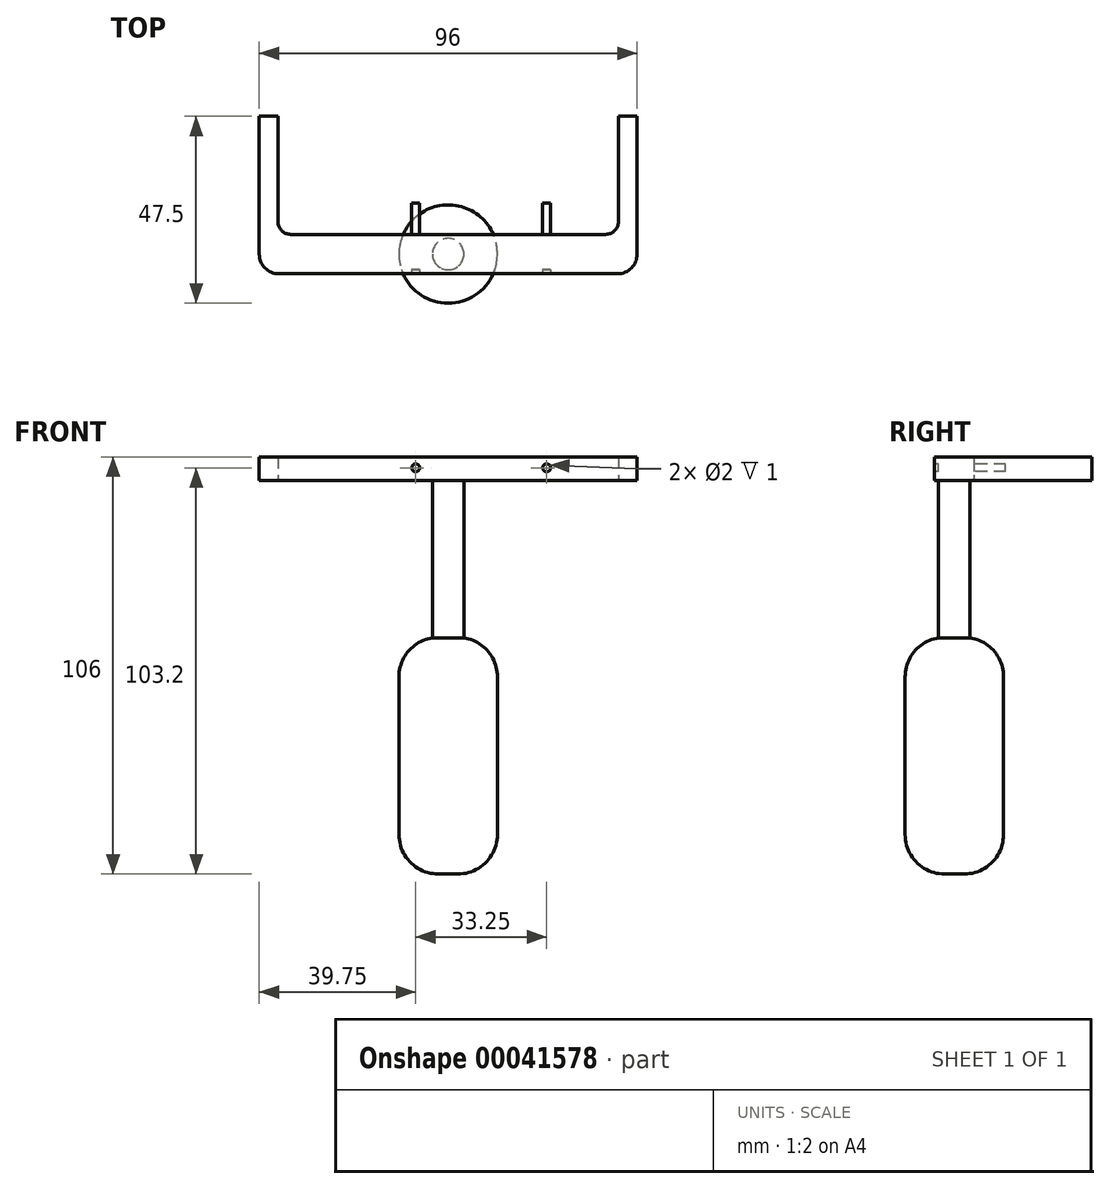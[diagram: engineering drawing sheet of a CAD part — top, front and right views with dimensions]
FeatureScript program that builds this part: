
annotation { "Feature Type Name" : "Feature", "Feature Type Description" : "" }
export const myFeature = defineFeature(function(context is Context, id is Id, definition is map)
    precondition{}
    {
        {
            var Q0;
            Q0=qCreatedBy(makeId("Top.planeOp"),FACE);
            var sketch = newSketch(context, id + "F0", { "sketchPlane" : qUnion([Q0])});
            skLineSegment(sketch, "E0.top", {"start": v(-48, -45) * mm, "end": v(48, -45) * mm});
            skLineSegment(sketch, "E0.left", {"start": v(-48, -5) * mm, "end": v(-48, -45) * mm});
            skLineSegment(sketch, "E0.right", {"start": v(48, -5) * mm, "end": v(48, -45) * mm});
            skLineSegment(sketch, "E1.top", {"start": v(-43.25, -35) * mm, "end": v(43.25, -35) * mm});
            skLineSegment(sketch, "E1.left", {"start": v(-43.25, -5) * mm, "end": v(-43.25, -35) * mm});
            skLineSegment(sketch, "E1.right", {"start": v(43.25, -5) * mm, "end": v(43.25, -35) * mm});
            skLineSegment(sketch, "E2", {"start": v(-43.25, -5) * mm, "end": v(-48, -5) * mm});
            skLineSegment(sketch, "E3", {"start": v(43.25, -5) * mm, "end": v(48, -5) * mm});
            skSolve(sketch);
        }
        {
            var Q0;
            Q0=makeQuery(id+"F0.imprint","IMPRINT",FACE,{"disambiguationData":[TD([[makeQuery(id+"F0.imprint","IMPRINT",EDGE,{"derivedFrom":sQuery(id+"F0.wireOp",EDGE,"E0.top")}),1.0]])]});
            extrude(context, id + "F1", {"entities" : qUnion([Q0]), "depth" : 6 * mm});
        }
        {
            var Q0;
            Q0=makeQuery(id+"F1.opExtrude","SWEPT_EDGE",EDGE,{"disambiguationData":[OSD([sQuery(id+"F0.wireOp",EDGE,"E1.top"),sQuery(id+"F0.wireOp",EDGE,"E1.left")])]});
            var Q1;
            Q1=makeQuery(id+"F1.opExtrude","SWEPT_EDGE",EDGE,{"disambiguationData":[OSD([sQuery(id+"F0.wireOp",EDGE,"E1.top"),sQuery(id+"F0.wireOp",EDGE,"E1.right")])]});
            fillet(context, id + "F2", {"entities" : qUnion([Q0, Q1]), "radius" : 3.25 * mm, "tangentPropagation" : true, "allowEdgeOverflow" : false});
        }
        {
            var Q0;
            Q0=makeQuery(id+"F1.opExtrude","SWEPT_EDGE",EDGE,{"disambiguationData":[OSD([sQuery(id+"F0.wireOp",EDGE,"E0.top"),sQuery(id+"F0.wireOp",EDGE,"E0.right")])]});
            var Q1;
            Q1=makeQuery(id+"F1.opExtrude","SWEPT_EDGE",EDGE,{"disambiguationData":[OSD([sQuery(id+"F0.wireOp",EDGE,"E0.top"),sQuery(id+"F0.wireOp",EDGE,"E0.left")])]});
            fillet(context, id + "F3", {"entities" : qUnion([Q0, Q1]), "radius" : 5 * mm, "tangentPropagation" : true, "allowEdgeOverflow" : false});
        }
        {
            var Q0;
            Q0=makeQuery(id+"F1.opExtrude","SWEPT_FACE",FACE,{"disambiguationData":[OSD([sQuery(id+"F0.wireOp",EDGE,"E0.top")])]});
            var sketch = newSketch(context, id + "F4", { "sketchPlane" : qUnion([Q0])});
            skCircle(sketch, "E4", {"center": v(-8.25, 3.2) * mm, "radius": 1 * mm});
            skCircle(sketch, "E5", {"center": v(25, 3.2) * mm, "radius": 1 * mm});
            skSolve(sketch);
        }
        {
            var Q0;
            Q0=makeQuery(id+"F4.imprint","IMPRINT",FACE,{"disambiguationData":[TD([[makeQuery(id+"F4.imprint","IMPRINT",EDGE,{"derivedFrom":sQuery(id+"F4.wireOp",EDGE,"E4")}),1.0]])]});
            var Q1;
            Q1=makeQuery(id+"F4.imprint","IMPRINT",FACE,{"disambiguationData":[TD([[makeQuery(id+"F4.imprint","IMPRINT",EDGE,{"derivedFrom":sQuery(id+"F4.wireOp",EDGE,"E5")}),1.0]])]});
            var Q2;
            Q2=sQuery(id+"F4.wireOp",EDGE,"E4");
            var Q3;
            Q3=sQuery(id+"F4.wireOp",EDGE,"E5");
            extrude(context, id + "F5", {"entities" : qUnion([Q0, Q1]), "operationType" : NewBodyOperationType.REMOVE, "surfaceEntities" : qUnion([Q2, Q3]), "oppositeDirection" : true, "depth" : 10 * mm});
        }
        {
            var Q0;
            Q0=makeQuery(id+"F1.opExtrude","CAP_FACE",FACE,{"disambiguationData":[OSD([sQuery(id+"F0.wireOp",EDGE,"E0.top"),sQuery(id+"F0.wireOp",EDGE,"E0.left"),sQuery(id+"F0.wireOp",EDGE,"E0.right"),sQuery(id+"F0.wireOp",EDGE,"E1.top"),sQuery(id+"F0.wireOp",EDGE,"E1.left"),sQuery(id+"F0.wireOp",EDGE,"E1.right"),sQuery(id+"F0.wireOp",EDGE,"E2"),sQuery(id+"F0.wireOp",EDGE,"E3")])],"isStart":true});
            var sketch = newSketch(context, id + "F6", { "sketchPlane" : qUnion([Q0])});
            skCircle(sketch, "E6", {"center": v(0, 40) * mm, "radius": 4 * mm});
            skSolve(sketch);
        }
        {
            var Q0;
            Q0=makeQuery(id+"F6.imprint","IMPRINT",FACE,{"disambiguationData":[TD([[makeQuery(id+"F6.imprint","IMPRINT",EDGE,{"derivedFrom":sQuery(id+"F6.wireOp",EDGE,"E6")}),1.0]])]});
            extrude(context, id + "F7", {"entities" : qUnion([Q0]), "operationType" : NewBodyOperationType.ADD, "depth" : 40 * mm});
        }
        {
            var Q0;
            Q0=makeQuery(id+"F7.opExtrude","CAP_FACE",FACE,{"disambiguationData":[OSD([sQuery(id+"F6.wireOp",EDGE,"E6")])],"isStart":false});
            var sketch = newSketch(context, id + "F8", { "sketchPlane" : qUnion([Q0])});
            skCircle(sketch, "E7", {"center": v(0, 40) * mm, "radius": 12.5 * mm});
            skSolve(sketch);
        }
        {
            var Q0;
            Q0=makeQuery(id+"F8.imprint","IMPRINT",FACE,{"disambiguationData":[TD([[makeQuery(id+"F8.imprint","IMPRINT",EDGE,{"derivedFrom":makeQuery(id+"F7.opExtrude","CAP_EDGE",EDGE,{"disambiguationData":[OSD([sQuery(id+"F6.wireOp",EDGE,"E6")])],"isStart":false})}),1.0]])]});
            var Q1;
            Q1=makeQuery(id+"F8.imprint","IMPRINT",FACE,{"disambiguationData":[TD([[makeQuery(id+"F8.imprint","IMPRINT",EDGE,{"derivedFrom":sQuery(id+"F8.wireOp",EDGE,"E7")}),1.0]])]});
            var Q2;
            Q2=sQuery(id+"F8.wireOp",EDGE,"E7");
            extrude(context, id + "F9", {"entities" : qUnion([Q0, Q1]), "operationType" : NewBodyOperationType.ADD, "surfaceEntities" : qUnion([Q2]), "depth" : 60 * mm});
        }
        {
            var Q0;
            Q0=makeQuery(id+"F9.opExtrude","CAP_EDGE",EDGE,{"disambiguationData":[OSD([sQuery(id+"F8.wireOp",EDGE,"E7")])],"isStart":false});
            var Q1;
            Q1=makeQuery(id+"F9.opExtrude","CAP_EDGE",EDGE,{"disambiguationData":[OSD([sQuery(id+"F8.wireOp",EDGE,"E7")])],"isStart":true});
            fillet(context, id + "F10", {"entities" : qUnion([Q0, Q1]), "radius" : 10 * mm, "tangentPropagation" : true, "allowEdgeOverflow" : false});
        }
        {
            var Q0;
            Q0=makeQuery(id+"F1.opExtrude","SWEPT_FACE",FACE,{"disambiguationData":[OSD([sQuery(id+"F0.wireOp",EDGE,"E0.top")])]});
            cPlane(context, id + "F11", {"entities" : qUnion([Q0]), "cplaneType" : CPlaneType.OFFSET, "offset" : 1 * mm, "oppositeDirection" : true, "width" : 150 * mm, "height" : 150 * mm});
        }
        {
            var Q0;
            Q0=qCreatedBy(id+"F11.planeOp",FACE);
            var sketch = newSketch(context, id + "F12", { "sketchPlane" : qUnion([Q0])});
            skCircle(sketch, "E8", {"center": v(-8.25, 3.2) * mm, "radius": 1 * mm});
            skCircle(sketch, "E9", {"center": v(25, 3.2) * mm, "radius": 1 * mm});
            skSolve(sketch);
        }
        {
            var Q0;
            Q0=makeQuery(id+"F12.imprint","IMPRINT",FACE,{"disambiguationData":[TD([[makeQuery(id+"F12.imprint","IMPRINT",EDGE,{"derivedFrom":sQuery(id+"F12.wireOp",EDGE,"E8")}),1.0]])]});
            var Q1;
            Q1=makeQuery(id+"F12.imprint","IMPRINT",FACE,{"disambiguationData":[TD([[makeQuery(id+"F12.imprint","IMPRINT",EDGE,{"derivedFrom":sQuery(id+"F12.wireOp",EDGE,"E9")}),1.0]])]});
            extrude(context, id + "F13", {"entities" : qUnion([Q0, Q1]), "operationType" : NewBodyOperationType.ADD, "oppositeDirection" : true, "depth" : 17 * mm});
        }
    });
